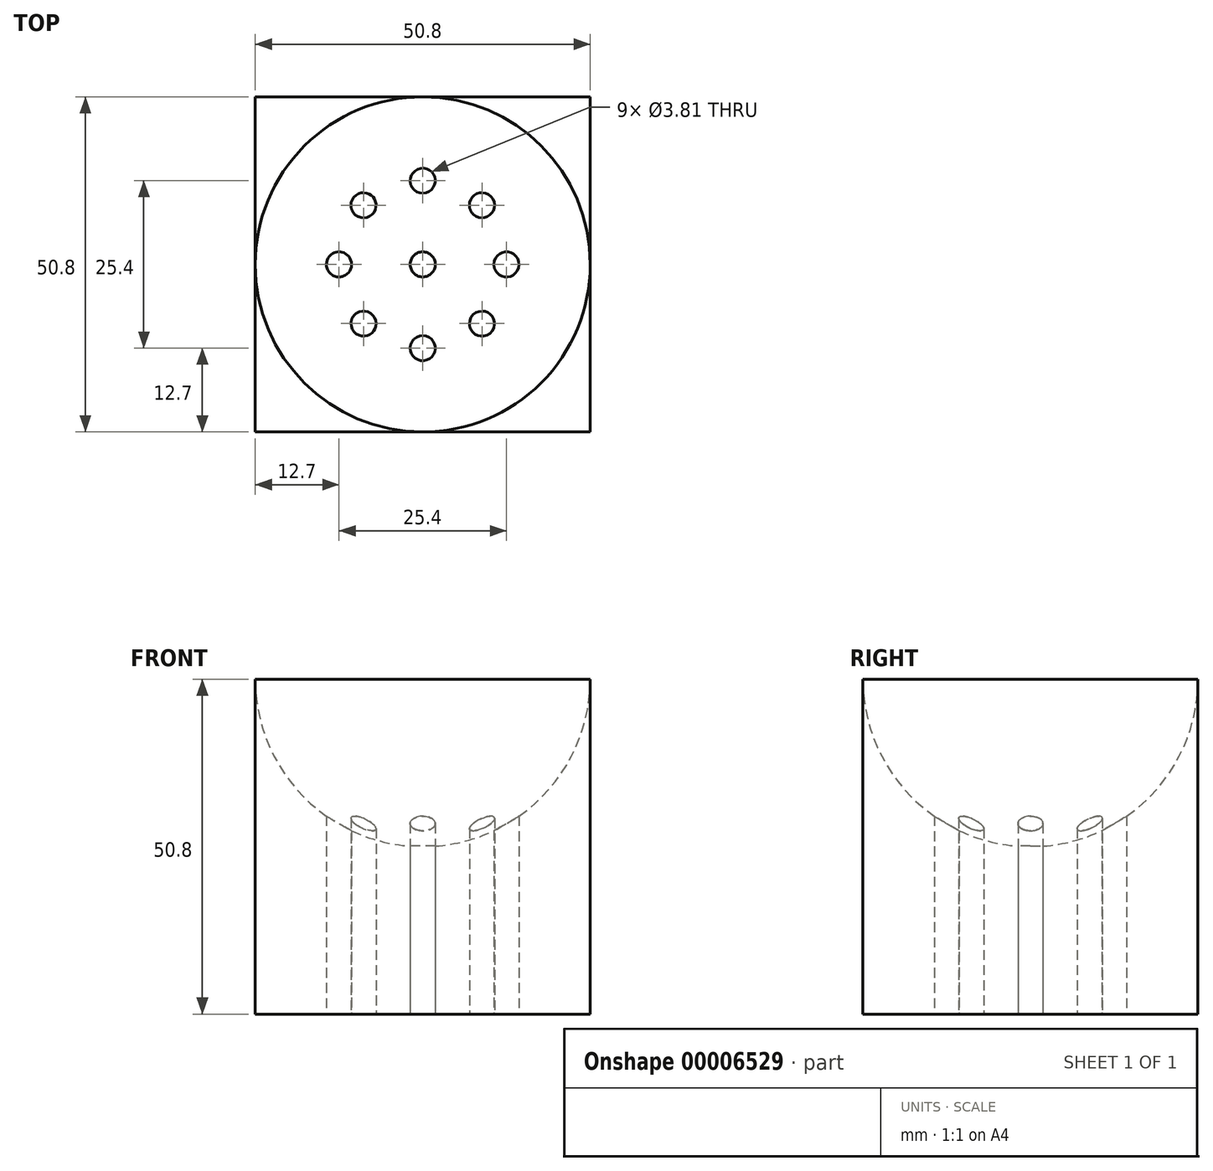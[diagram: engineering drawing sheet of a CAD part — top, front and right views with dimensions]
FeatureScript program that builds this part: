
annotation { "Feature Type Name" : "Feature", "Feature Type Description" : "" }
export const myFeature = defineFeature(function(context is Context, id is Id, definition is map)
    precondition{}
    {
        {
            var Q0;
            Q0=qCreatedBy(makeId("Top.planeOp"),FACE);
            var sketch = newSketch(context, id + "F0", { "sketchPlane" : qUnion([Q0])});
            skLineSegment(sketch, "E0.bottom", {"start": v(0, 0) * mm, "end": v(50.8, 0) * mm});
            skLineSegment(sketch, "E0.top", {"start": v(0, 50.8) * mm, "end": v(50.8, 50.8) * mm});
            skLineSegment(sketch, "E0.left", {"start": v(0, 0) * mm, "end": v(0, 50.8) * mm});
            skLineSegment(sketch, "E0.right", {"start": v(50.8, 0) * mm, "end": v(50.8, 50.8) * mm});
            skSolve(sketch);
        }
        {
            var Q0;
            Q0=makeQuery(id+"F0.imprint","IMPRINT",FACE,{"disambiguationData":[TD([[makeQuery(id+"F0.imprint","IMPRINT",EDGE,{"derivedFrom":sQuery(id+"F0.wireOp",EDGE,"E0.bottom")}),1.0]])]});
            extrude(context, id + "F1", {"entities" : qUnion([Q0]), "endBound" : BoundingType.SYMMETRIC, "depth" : 50.8 * mm});
        }
        {
            var Q0;
            Q0=makeQuery(id+"F1.opExtrude","CAP_FACE",FACE,{"disambiguationData":[OSD([sQuery(id+"F0.wireOp",EDGE,"E0.bottom"),sQuery(id+"F0.wireOp",EDGE,"E0.top"),sQuery(id+"F0.wireOp",EDGE,"E0.left"),sQuery(id+"F0.wireOp",EDGE,"E0.right")])],"isStart":false});
            var sketch = newSketch(context, id + "F2", { "sketchPlane" : qUnion([Q0])});
            skLineSegment(sketch, "E1", {"start": v(0, 0) * mm, "end": v(50.8, 50.8) * mm});
            skLineSegment(sketch, "E2", {"start": v(50.8, 50.8) * mm, "end": v(0, 50.8) * mm});
            skLineSegment(sketch, "E3", {"start": v(0, 50.8) * mm, "end": v(50.8, 0) * mm});
            skCircle(sketch, "E4", {"center": v(25.4, 25.4) * mm, "radius": 25.4 * mm});
            skSolve(sketch);
        }
        {
            var Q0;
            {var subQ1=sQuery(id+"F2.wireOp",EDGE,"E1");var subQ4=sQuery(id+"F2.wireOp",EDGE,"E3");var subQ6=makeQuery(id+"F2.imprint","INTERSECT",VERTEX,{"derivedFrom":[subQ1,subQ4]});Q0=makeQuery(id+"F2.imprint","IMPRINT",FACE,{"disambiguationData":[TD([[makeQuery(id+"F2.imprint","IMPRINT",EDGE,{"disambiguationData":[TD([[subQ6,-1.0]])],"derivedFrom":subQ1}),1.0]])]});}
            var Q1;
            {var subQ2=sQuery(id+"F2.wireOp",EDGE,"E3");var subQ4=sQuery(id+"F2.wireOp",EDGE,"E1");var subQ6=makeQuery(id+"F2.imprint","INTERSECT",VERTEX,{"derivedFrom":[subQ4,subQ2]});Q1=makeQuery(id+"F2.imprint","IMPRINT",FACE,{"disambiguationData":[TD([[makeQuery(id+"F2.imprint","IMPRINT",EDGE,{"disambiguationData":[TD([[subQ6,-1.0]])],"derivedFrom":subQ4}),-1.0]])]});}
            var Q2;
            Q2=sQuery(id+"F2.wireOp",EDGE,"E3");
            revolve(context, id + "F3", {"operationType" : NewBodyOperationType.REMOVE, "entities" : qUnion([Q0, Q1]), "axis" : qUnion([Q2]), "revolveType" : RevolveType.FULL, "oppositeDirection" : true});
        }
        {
            var Q0;
            Q0=makeQuery(id+"F1.opExtrude","CAP_FACE",FACE,{"disambiguationData":[OSD([sQuery(id+"F0.wireOp",EDGE,"E0.bottom"),sQuery(id+"F0.wireOp",EDGE,"E0.top"),sQuery(id+"F0.wireOp",EDGE,"E0.left"),sQuery(id+"F0.wireOp",EDGE,"E0.right")])],"isStart":true});
            var sketch = newSketch(context, id + "F4", { "sketchPlane" : qUnion([Q0])});
            skLineSegment(sketch, "E5", {"start": v(0, 0) * mm, "end": v(50.8, -50.8) * mm, "construction": true});
            skLineSegment(sketch, "E6", {"start": v(50.8, -50.8) * mm, "end": v(50.8, 0) * mm});
            skLineSegment(sketch, "E7", {"start": v(50.8, 0) * mm, "end": v(0, -50.8) * mm, "construction": true});
            skCircle(sketch, "E8", {"center": v(25.4, -25.4) * mm, "radius": 1.9 * mm});
            skLineSegment(sketch, "E9", {"start": v(0, -25.4) * mm, "end": v(50.8, -25.4) * mm, "construction": true});
            skCircle(sketch, "E10", {"center": v(38.1, -25.4) * mm, "radius": 1.9 * mm});
            skCircle(sketch, "E11.1.0", {"center": v(34.38, -16.42) * mm, "radius": 1.9 * mm});
            skCircle(sketch, "E11.2.0", {"center": v(25.4, -12.7) * mm, "radius": 1.9 * mm});
            skCircle(sketch, "E11.3.0", {"center": v(16.42, -16.42) * mm, "radius": 1.9 * mm});
            skCircle(sketch, "E11.4.0", {"center": v(12.7, -25.4) * mm, "radius": 1.9 * mm});
            skCircle(sketch, "E11.5.0", {"center": v(16.42, -34.38) * mm, "radius": 1.9 * mm});
            skCircle(sketch, "E11.6.0", {"center": v(25.4, -38.1) * mm, "radius": 1.9 * mm});
            skCircle(sketch, "E11.7.0", {"center": v(34.38, -34.38) * mm, "radius": 1.9 * mm});
            skSolve(sketch);
        }
        {
            var Q0;
            {Q0=qUnion([makeQuery(id+"F4.imprint","IMPRINT",FACE,{"disambiguationData":[TD([[makeQuery(id+"F4.imprint","IMPRINT",EDGE,{"derivedFrom":sQuery(id+"F4.wireOp",EDGE,"E8")}),1.0]])]}),makeQuery(id+"F4.imprint","IMPRINT",FACE,{"disambiguationData":[TD([[makeQuery(id+"F4.imprint","IMPRINT",EDGE,{"derivedFrom":sQuery(id+"F4.wireOp",EDGE,"E10")}),1.0]])]}),makeQuery(id+"F4.imprint","IMPRINT",FACE,{"disambiguationData":[TD([[makeQuery(id+"F4.imprint","IMPRINT",EDGE,{"derivedFrom":sQuery(id+"F4.wireOp",EDGE,"E11.1.0")}),1.0]])]}),makeQuery(id+"F4.imprint","IMPRINT",FACE,{"disambiguationData":[TD([[makeQuery(id+"F4.imprint","IMPRINT",EDGE,{"derivedFrom":sQuery(id+"F4.wireOp",EDGE,"E11.2.0")}),1.0]])]}),makeQuery(id+"F4.imprint","IMPRINT",FACE,{"disambiguationData":[TD([[makeQuery(id+"F4.imprint","IMPRINT",EDGE,{"derivedFrom":sQuery(id+"F4.wireOp",EDGE,"E11.3.0")}),1.0]])]}),makeQuery(id+"F4.imprint","IMPRINT",FACE,{"disambiguationData":[TD([[makeQuery(id+"F4.imprint","IMPRINT",EDGE,{"derivedFrom":sQuery(id+"F4.wireOp",EDGE,"E11.4.0")}),1.0]])]}),makeQuery(id+"F4.imprint","IMPRINT",FACE,{"disambiguationData":[TD([[makeQuery(id+"F4.imprint","IMPRINT",EDGE,{"derivedFrom":sQuery(id+"F4.wireOp",EDGE,"E11.5.0")}),1.0]])]}),makeQuery(id+"F4.imprint","IMPRINT",FACE,{"disambiguationData":[TD([[makeQuery(id+"F4.imprint","IMPRINT",EDGE,{"derivedFrom":sQuery(id+"F4.wireOp",EDGE,"E11.6.0")}),1.0]])]}),makeQuery(id+"F4.imprint","IMPRINT",FACE,{"disambiguationData":[TD([[makeQuery(id+"F4.imprint","IMPRINT",EDGE,{"derivedFrom":sQuery(id+"F4.wireOp",EDGE,"E11.7.0")}),1.0]])]})]);}
            extrude(context, id + "F5", {"entities" : qUnion([Q0]), "operationType" : NewBodyOperationType.REMOVE, "endBound" : BoundingType.THROUGH_ALL, "oppositeDirection" : true, "depth" : 25.4 * mm});
        }
    });
